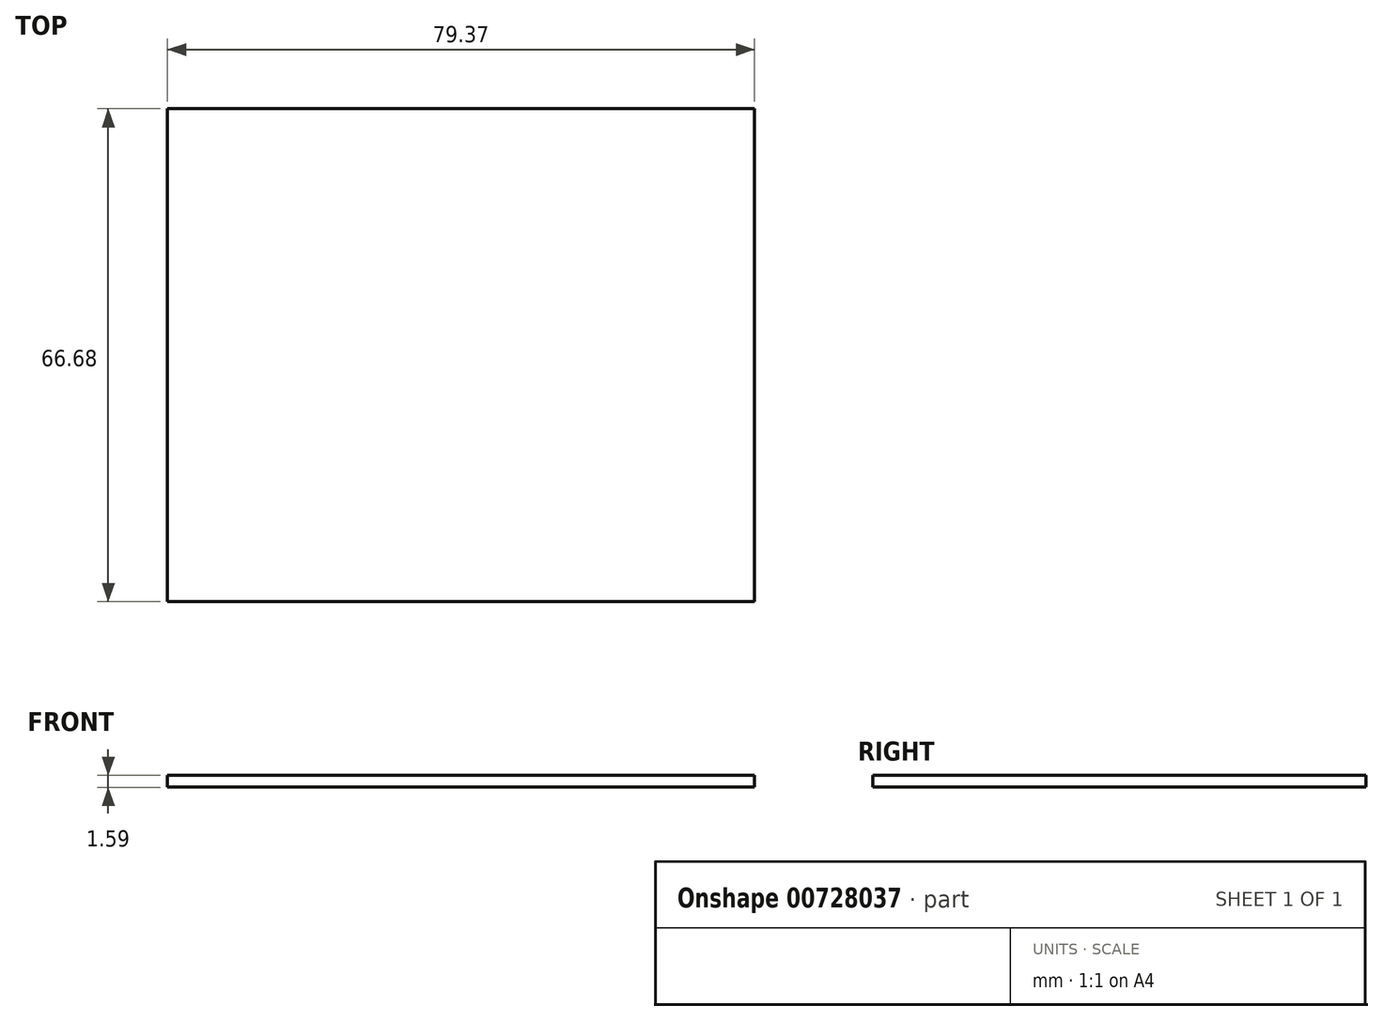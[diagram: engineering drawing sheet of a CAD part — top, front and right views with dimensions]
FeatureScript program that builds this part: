
annotation { "Feature Type Name" : "Feature", "Feature Type Description" : "" }
export const myFeature = defineFeature(function(context is Context, id is Id, definition is map)
    precondition{}
    {
        {
            var Q0;
            Q0=qCreatedBy(makeId("Top.planeOp"),FACE);
            var sketch = newSketch(context, id + "F0", { "sketchPlane" : qUnion([Q0])});
            skLineSegment(sketch, "E0.bottom", {"start": v(-41.67, 33.34) * mm, "end": v(37.7, 33.34) * mm});
            skLineSegment(sketch, "E0.top", {"start": v(-41.67, -33.34) * mm, "end": v(37.7, -33.34) * mm});
            skLineSegment(sketch, "E0.left", {"start": v(-41.67, 33.34) * mm, "end": v(-41.67, -33.34) * mm});
            skLineSegment(sketch, "E0.right", {"start": v(37.7, 33.34) * mm, "end": v(37.7, -33.34) * mm});
            skSolve(sketch);
        }
        {
            var Q0;
            Q0 = qSketchRegion(id + "F0", true);
            extrude(context, id + "F1", {"entities" : qUnion([Q0]), "oppositeDirection" : true, "depth" : 1.59 * mm, "offsetDistance" : 25.4 * mm});
        }
    });
